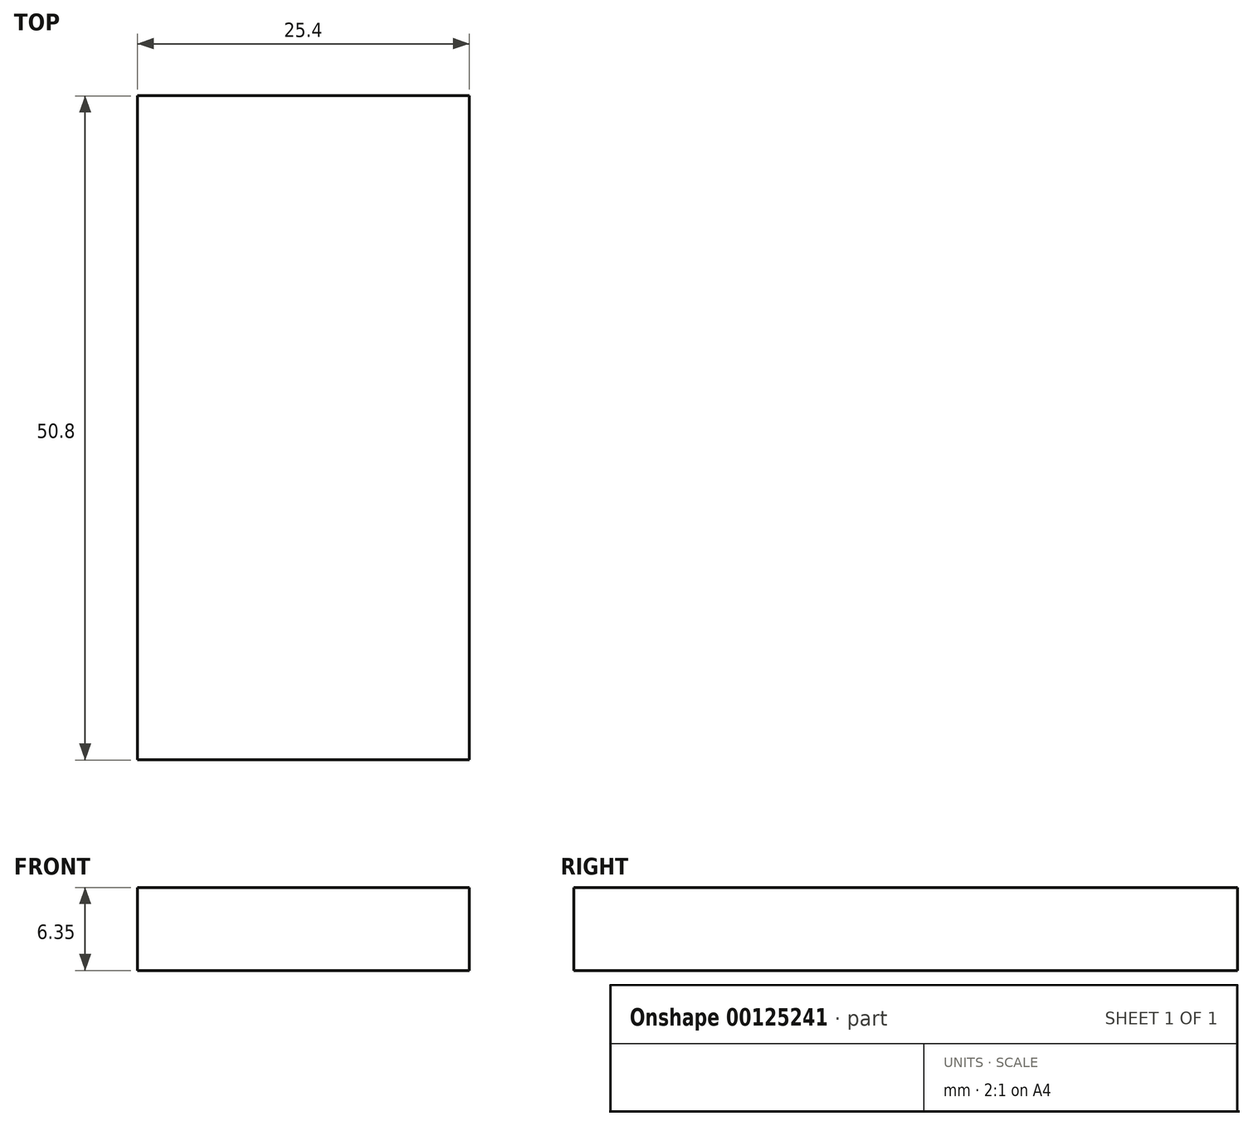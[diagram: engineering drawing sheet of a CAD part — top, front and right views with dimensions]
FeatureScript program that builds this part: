
annotation { "Feature Type Name" : "Feature", "Feature Type Description" : "" }
export const myFeature = defineFeature(function(context is Context, id is Id, definition is map)
    precondition{}
    {
        {
            var Q0;
            Q0=qCreatedBy(makeId("Top.planeOp"),FACE);
            var sketch = newSketch(context, id + "F0", { "sketchPlane" : qUnion([Q0])});
            skLineSegment(sketch, "E0.bottom", {"start": v(-25.12, 12.04) * mm, "end": v(0.28, 12.04) * mm});
            skLineSegment(sketch, "E0.top", {"start": v(-25.12, -38.76) * mm, "end": v(0.28, -38.76) * mm});
            skLineSegment(sketch, "E0.left", {"start": v(-25.12, 12.04) * mm, "end": v(-25.12, -38.76) * mm});
            skLineSegment(sketch, "E0.right", {"start": v(0.28, 12.04) * mm, "end": v(0.28, -38.76) * mm});
            skSolve(sketch);
        }
        {
            var Q0;
            Q0=makeQuery(id+"F0.imprint","IMPRINT",FACE,{"disambiguationData":[TD([[makeQuery(id+"F0.imprint","IMPRINT",EDGE,{"derivedFrom":sQuery(id+"F0.wireOp",EDGE,"E0.bottom")}),-1.0]])]});
            extrude(context, id + "F1", {"entities" : qUnion([Q0]), "depth" : 6.35 * mm});
        }
    });
